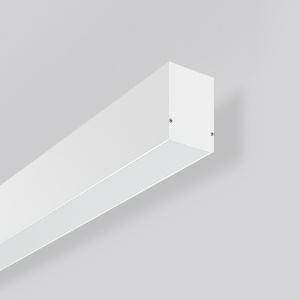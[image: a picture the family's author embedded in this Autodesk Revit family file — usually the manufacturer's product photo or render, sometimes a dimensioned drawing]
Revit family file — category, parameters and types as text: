
# Revit family: less_is_more_50_312609_002_76_a3f8
name_source: partatom
category: Lighting Fixtures
units: mm (PartAtom-declared; Revit-internal decimal feet)

## family parameters
Cut with Voids When Loaded = No
Host = Face
Light Source = No
Part Type = Normal
Room Calculation Point = No
Round Connector Dimension = Use Diameter
Shared = No

## types (1)
- LESS IS MORE 50 (1 x LED Modul 830, 1850 lm, 3000)
    Apparent Load = 16 VA
    CIE Flux Codes = 48 80 96 100 100
    Color Rendering = 80
    Color Temperature = 3000
    Default Elevation = 1800 mm
    Description = Series: LESS IS MORE 50
Linear wall luminaires. Housing: extruded aluminium profile, powder-coated. End cap aluminium powder-coated. Diffuser made of non-yellowing plastic (PMMA), opal. Direct light emission. Suitable for Wall (surface). LED unit with integrated converter interchangeable and removable. Suitable for through-wiring. With sensors or as a safety luminaire on request. 
Colour: traffic white, matt (RAL 9016)
Length: 1407 mm
Width: 67 mm
Height: 75 mm
Lamp: LED
Socket: without socket
Colour temperature: 3000K
Colour rendering index (CRI): 80
System power: 16 W
Rated luminous flux: 1850 lm
Luminous efficiency: 116 lm/W
Control gear: Converter, dimmable, DALI
Protection class: I
Type of protection: IP 20
    Height = 75 mm
    Lamp = 1 x LED Modul 830
    Lamp Light Flux = 1850 lm
    Lamp count = 1
    Length = 1407 mm
    Lifetime = 50000 h
    Luminous efficacy = 116 lm/W
    Manufacturer = RZB
    ModVariant = No
    Model = 312609.002.76
    Mounting Place = Wall
    Mounting Type = Surface mounted
    Number of Poles = 1
    OnlyDefault = Yes
    Power Factor = 1
    Product Name = LESS IS MORE 50
    Product group = Surface mounted LED linear luminaires
    ProductGroupID = 2007
    Protection Class = Protection class I
    Protection Degree = IP 20
    RLX_Detail_Level = 1
    RLX_Emergency_Light_Flux = 0 lm
    RLX_Emergency_Type = 0
    RLX_Emergency_Type_DB = No
    RlxData = <blob elided: 35137 chars, md5=3c92e3fc>
    Socket = socket
    Standby Power = 0 W
    System Light Flux = 1850 lm
    System Power = 16 W
    Type Comments = Product without accessories
    Type Image = 312606.002.jpg
    URL = http://relux.com
    VarID = ---
    Voltage = 0 V
    Weight = 0.00 kg
    Width = 67 mm

## geometry (parser evidence)
native form markers: Blend x4, Sweep x9
no freeform markers — native parametric forms only
